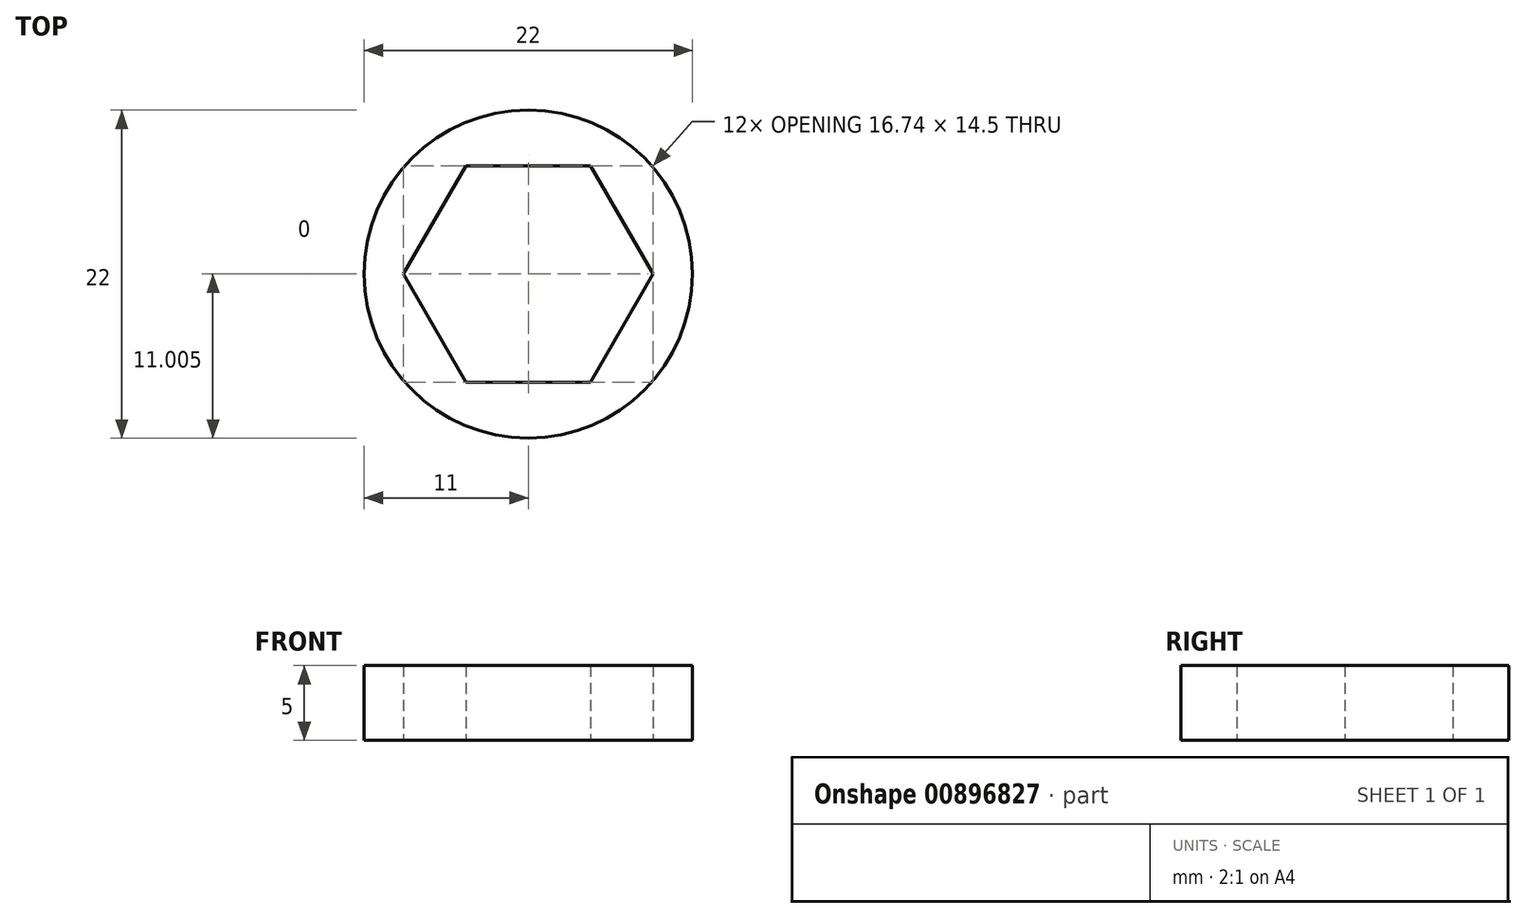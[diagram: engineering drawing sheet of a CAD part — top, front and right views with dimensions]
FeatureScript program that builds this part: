
annotation { "Feature Type Name" : "Feature", "Feature Type Description" : "" }
export const myFeature = defineFeature(function(context is Context, id is Id, definition is map)
    precondition{}
    {
        {
            var Q0;
            Q0=qCreatedBy(makeId("Top.planeOp"),FACE);
            var sketch = newSketch(context, id + "F0", { "sketchPlane" : qUnion([Q0])});
            skCircle(sketch, "E0.cCircle", {"center": v(1.1, 28.3) * mm, "radius": 7.25 * mm, "construction": true});
            skLineSegment(sketch, "E0.0", {"start": v(-3.08, 35.54) * mm, "end": v(5.3, 35.54) * mm});
            skLineSegment(sketch, "E0.1", {"start": v(5.3, 35.54) * mm, "end": v(9.48, 28.3) * mm});
            skLineSegment(sketch, "E0.2", {"start": v(9.48, 28.3) * mm, "end": v(5.3, 21.04) * mm});
            skLineSegment(sketch, "E0.3", {"start": v(5.3, 21.04) * mm, "end": v(-3.08, 21.04) * mm});
            skLineSegment(sketch, "E0.4", {"start": v(-3.08, 21.04) * mm, "end": v(-7.26, 28.3) * mm});
            skLineSegment(sketch, "E0.5", {"start": v(-7.26, 28.3) * mm, "end": v(-3.08, 35.54) * mm});
            skPoint(sketch, "E0.0.midPoint", {"position": v(1.1, 35.54) * mm});
            skCircle(sketch, "E1", {"center": v(1.1, 28.3) * mm, "radius": 11 * mm});
            skSolve(sketch);
        }
        {
            var Q0;
            Q0=qSketchRegion(id+"F0",true);
            extrude(context, id + "F1", {"entities" : qUnion([Q0]), "depth" : 5 * mm, "offsetDistance" : 25.4 * mm});
        }
    });
